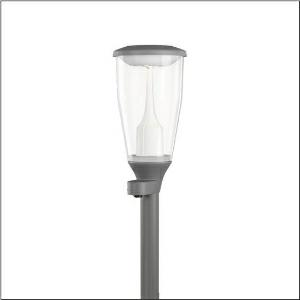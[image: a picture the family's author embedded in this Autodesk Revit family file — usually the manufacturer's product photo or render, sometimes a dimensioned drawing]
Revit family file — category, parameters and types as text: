
# Revit family: dl_11_iq___st1_2a_5xa5565eu14h000022_1a9b
name_source: partatom
category: Lighting Fixtures
units: mm (PartAtom-declared; Revit-internal decimal feet)

## family parameters
Cut with Voids When Loaded = No
Host = Face
Light Source = No
Part Type = Normal
Room Calculation Point = No
Round Connector Dimension = Use Diameter
Shared = No

## types (1)
- --- (1 x LED, 1560 lm, 10.7 W, 3000K)
    Apparent Load = 11 VA
    CIE Flux Codes = 24 63 94 96 100
    Color Rendering = 70
    Color Temperature = 3000K
    Default Elevation = 1800 mm
    Description = DL 11 iQ, mast luminaire, Module 540 iQ-SR, primary light control with 3 zone facetted reflector, of plastic, silver coated, highly specular, structured, primary optical cover: cover, of PMMA, transparent, light distribution: ST1.2a, light emission: direct distribution, primary light characteristic: asymmetric, installation type: post-top, LED, High Power LED, rated luminous flux: 1.560lm, luminous efficacy: 146lm/W, light colour: 730, colour temperature: 3000K, control gear: iQ-Street Remote, D4i with power reduction, control: pre-setting: logarithmic dimming characteristic, Street-Remote, Auto-Match, Temp-Guard, Lumen-Switch, Night-Set, Smart-Wire, Light-Fading, Desk-Remote (wireless, voltage-free reading and setting of iQ features in the workshop via application-optimized NFC function/RFID function), optimised constant luminous flux control (CLO 2.0), mains connection: 220..240V, AC, 50/60Hz, connection cable pre-assembled, cable length: 5,5m, start of lifetime: 11W, end of service life: 11W, reduction: 6W, luminaire housing, upper part, of diecast aluminium, coated, Siteco® metallic grey (DB 702S), spigot size: 60mm (post-top), mounting height: 3..5m, post-top mast mounting element, of diecast aluminium, coated, Siteco® metallic grey (DB 702S), Module 540 iQ-SR, traffic white (RAL 9016), equipment: standard, Smart Interface below, protection rating (complete): IP66, insulation class (complete): insulation class II (safety insulation), certification: CE, ENEC, ENEC+, VDE, impact resistance: IK07, packaging unit: 1 piece

Light Distribution: ST1.2a
    Height = 665 mm
    Lamp = 1 x LED
    Lamp Light Flux = 1560 lm
    Lamp Power = 10.7 W
    Lamp count = 1
    Length = 334 mm
    Luminous efficacy = 146 lm/W
    Manufacturer = Siteco
    ModVariant = No
    Model = 5XA5565EU14H000022
    Number of Poles = 1
    OnlyDefault = Yes
    Power Factor = 1
    Product Name = DL 11 iQ | ST1.2a
    Product group = mast luminaire | pylon top
    ProductGroupID = 6100
    Protection Class = Protection class II
    Protection Degree = IP 66
    RLX_Detail_Level = 1
    RLX_Emergency_Light_Flux = 0 lm
    RLX_Emergency_Type = 0
    RLX_Emergency_Type_DB = No
    RlxData = <blob elided: 158661 chars, md5=86b1b088>
    Socket = socket
    Standby Power = 0 W
    System Light Flux = 1560 lm
    System Power = 11 W
    Type Comments = factory setting: luminous flux: 100 % | dim-lin: 254 | 419 mA
    Type Image = l_1337539.jpg
    URL = http://relux.com
    VarID = @adj_095070
    Voltage = 0 V
    Weight = 0.00 kg
    Width = 0 mm  [stored 0 ft]

note: [stored X ft] marks values corroborated as IEEE doubles in the binary element streams (Revit-internal decimal feet)

## geometry (parser evidence)
native form markers: Blend x4, Sweep x14
no freeform markers — native parametric forms only
